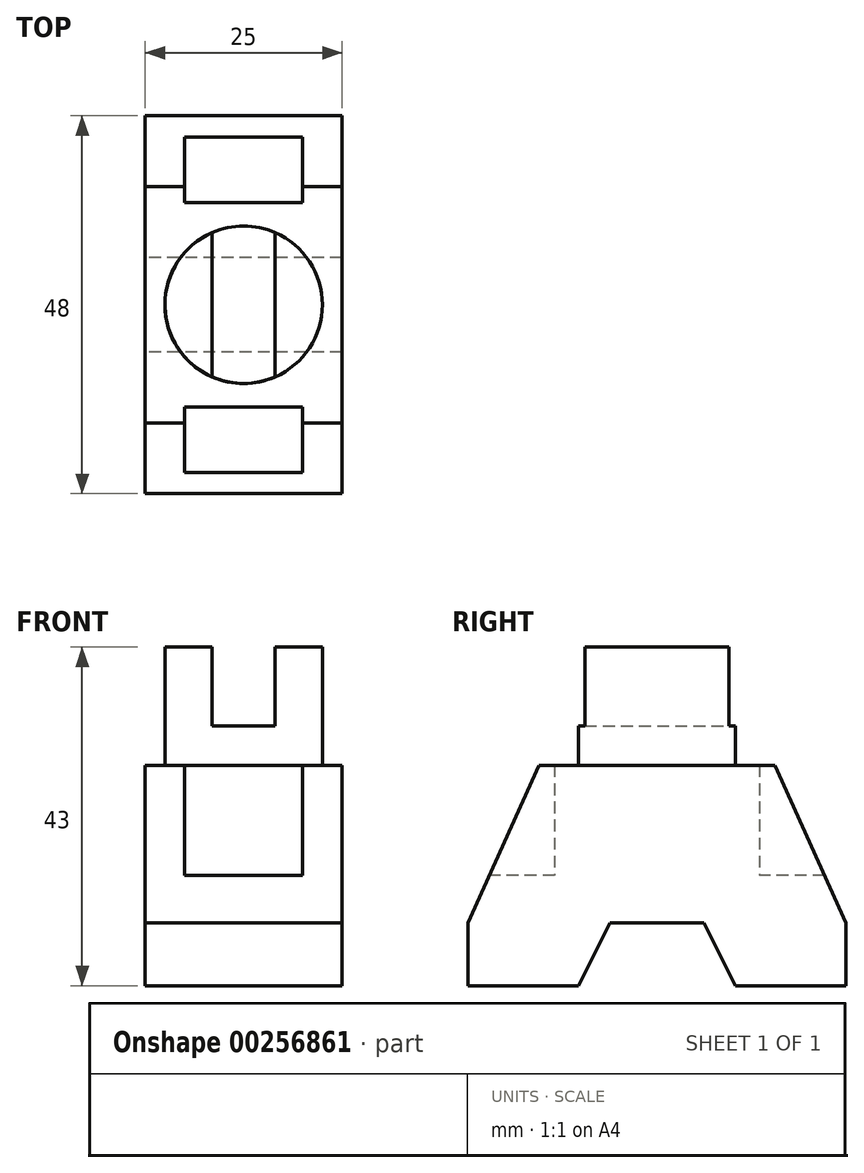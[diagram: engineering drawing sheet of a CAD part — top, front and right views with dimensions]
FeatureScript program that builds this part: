
annotation { "Feature Type Name" : "Feature", "Feature Type Description" : "" }
export const myFeature = defineFeature(function(context is Context, id is Id, definition is map)
    precondition{}
    {
        {
            var Q0;
            Q0=qCreatedBy(makeId("Right.planeOp"),FACE);
            var sketch = newSketch(context, id + "F0", { "sketchPlane" : qUnion([Q0])});
            skLineSegment(sketch, "E0.bottom", {"start": v(24, 14) * mm, "end": v(-24, 14) * mm});
            skLineSegment(sketch, "E0.top", {"start": v(24, -14) * mm, "end": v(-24, -14) * mm});
            skLineSegment(sketch, "E0.left", {"start": v(24, 14) * mm, "end": v(24, -14) * mm});
            skLineSegment(sketch, "E0.right", {"start": v(-24, 14) * mm, "end": v(-24, -14) * mm});
            skPoint(sketch, "E0.middle", {"position": v(0, 0) * mm});
            skLineSegment(sketch, "E1", {"start": v(-15, 14) * mm, "end": v(-15, -14) * mm});
            skLineSegment(sketch, "E2", {"start": v(-10, 14) * mm, "end": v(-10, -14) * mm});
            skLineSegment(sketch, "E3", {"start": v(15, 14) * mm, "end": v(15, -14) * mm});
            skLineSegment(sketch, "E4", {"start": v(10, 14) * mm, "end": v(10, -14) * mm});
            skLineSegment(sketch, "E5", {"start": v(-24, -4) * mm, "end": v(24, -4) * mm});
            skLineSegment(sketch, "E6", {"start": v(-24, -6) * mm, "end": v(24, -6) * mm});
            skLineSegment(sketch, "E7", {"start": v(-24, -6) * mm, "end": v(-15, 14) * mm});
            skLineSegment(sketch, "E8", {"start": v(24, -6) * mm, "end": v(15, 14) * mm});
            skLineSegment(sketch, "E9", {"start": v(-5, 14) * mm, "end": v(-5, -14) * mm});
            skLineSegment(sketch, "E10", {"start": v(5, 14) * mm, "end": v(5, -14) * mm});
            skLineSegment(sketch, "E11", {"start": v(-10, -14) * mm, "end": v(-5, -4) * mm});
            skLineSegment(sketch, "E12", {"start": v(10, -14) * mm, "end": v(5, -4) * mm});
            skSolve(sketch);
        }
        {
            var Q0;
            {var subQ0=sQuery(id+"F0.wireOp",EDGE,"E0.right");var subQ1=sQuery(id+"F0.wireOp",EDGE,"E0.top");var subQ2=makeQuery(id+"F0.imprint","INTERSECT",VERTEX,{"derivedFrom":[subQ1,subQ0]});Q0=makeQuery(id+"F0.imprint","IMPRINT",FACE,{"disambiguationData":[TD([[makeQuery(id+"F0.imprint","IMPRINT",EDGE,{"disambiguationData":[TD([[subQ2,1.0]])],"derivedFrom":subQ1}),-1.0]])]});}
            var Q1;
            {var subQ0=sQuery(id+"F0.wireOp",EDGE,"E5");var subQ1=sQuery(id+"F0.wireOp",EDGE,"E1");var subQ2=makeQuery(id+"F0.imprint","INTERSECT",VERTEX,{"derivedFrom":[subQ1,subQ0]});Q1=makeQuery(id+"F0.imprint","IMPRINT",FACE,{"disambiguationData":[TD([[makeQuery(id+"F0.imprint","IMPRINT",EDGE,{"disambiguationData":[TD([[subQ2,-1.0]])],"derivedFrom":subQ1}),-1.0]])]});}
            var Q2;
            {var subQ1=sQuery(id+"F0.wireOp",EDGE,"E1");var subQ3=sQuery(id+"F0.wireOp",EDGE,"E5");var subQ4=makeQuery(id+"F0.imprint","INTERSECT",VERTEX,{"derivedFrom":[subQ1,subQ3]});Q2=makeQuery(id+"F0.imprint","IMPRINT",FACE,{"disambiguationData":[TD([[makeQuery(id+"F0.imprint","IMPRINT",EDGE,{"disambiguationData":[TD([[subQ4,1.0]])],"derivedFrom":subQ3}),1.0]])]});}
            var Q3;
            {var subQ1=sQuery(id+"F0.wireOp",EDGE,"E0.bottom");var subQ3=sQuery(id+"F0.wireOp",EDGE,"E2");var subQ4=makeQuery(id+"F0.imprint","INTERSECT",VERTEX,{"derivedFrom":[subQ1,subQ3]});Q3=makeQuery(id+"F0.imprint","IMPRINT",FACE,{"disambiguationData":[TD([[makeQuery(id+"F0.imprint","IMPRINT",EDGE,{"disambiguationData":[TD([[subQ4,-1.0]])],"derivedFrom":subQ3}),-1.0]])]});}
            var Q4;
            {var subQ0=sQuery(id+"F0.wireOp",EDGE,"E2");var subQ1=sQuery(id+"F0.wireOp",EDGE,"E0.bottom");var subQ2=makeQuery(id+"F0.imprint","INTERSECT",VERTEX,{"derivedFrom":[subQ1,subQ0]});Q4=makeQuery(id+"F0.imprint","IMPRINT",FACE,{"disambiguationData":[TD([[makeQuery(id+"F0.imprint","IMPRINT",EDGE,{"disambiguationData":[TD([[subQ2,1.0]])],"derivedFrom":subQ1}),1.0]])]});}
            var Q5;
            {var subQ0=sQuery(id+"F0.wireOp",EDGE,"E9");var subQ1=sQuery(id+"F0.wireOp",EDGE,"E0.bottom");var subQ2=makeQuery(id+"F0.imprint","INTERSECT",VERTEX,{"derivedFrom":[subQ1,subQ0]});Q5=makeQuery(id+"F0.imprint","IMPRINT",FACE,{"disambiguationData":[TD([[makeQuery(id+"F0.imprint","IMPRINT",EDGE,{"disambiguationData":[TD([[subQ2,1.0]])],"derivedFrom":subQ1}),1.0]])]});}
            var Q6;
            {var subQ0=sQuery(id+"F0.wireOp",EDGE,"E4");var subQ1=sQuery(id+"F0.wireOp",EDGE,"E0.bottom");var subQ2=makeQuery(id+"F0.imprint","INTERSECT",VERTEX,{"derivedFrom":[subQ1,subQ0]});Q6=makeQuery(id+"F0.imprint","IMPRINT",FACE,{"disambiguationData":[TD([[makeQuery(id+"F0.imprint","IMPRINT",EDGE,{"disambiguationData":[TD([[subQ2,-1.0]])],"derivedFrom":subQ1}),1.0]])]});}
            var Q7;
            {var subQ1=sQuery(id+"F0.wireOp",EDGE,"E0.bottom");var subQ3=sQuery(id+"F0.wireOp",EDGE,"E4");var subQ4=makeQuery(id+"F0.imprint","INTERSECT",VERTEX,{"derivedFrom":[subQ1,subQ3]});Q7=makeQuery(id+"F0.imprint","IMPRINT",FACE,{"disambiguationData":[TD([[makeQuery(id+"F0.imprint","IMPRINT",EDGE,{"disambiguationData":[TD([[subQ4,-1.0]])],"derivedFrom":subQ3}),1.0]])]});}
            var Q8;
            {var subQ1=sQuery(id+"F0.wireOp",EDGE,"E3");var subQ3=sQuery(id+"F0.wireOp",EDGE,"E5");var subQ4=makeQuery(id+"F0.imprint","INTERSECT",VERTEX,{"derivedFrom":[subQ1,subQ3]});Q8=makeQuery(id+"F0.imprint","IMPRINT",FACE,{"disambiguationData":[TD([[makeQuery(id+"F0.imprint","IMPRINT",EDGE,{"disambiguationData":[TD([[subQ4,-1.0]])],"derivedFrom":subQ3}),1.0]])]});}
            var Q9;
            {var subQ0=sQuery(id+"F0.wireOp",EDGE,"E5");var subQ1=sQuery(id+"F0.wireOp",EDGE,"E3");var subQ2=makeQuery(id+"F0.imprint","INTERSECT",VERTEX,{"derivedFrom":[subQ1,subQ0]});Q9=makeQuery(id+"F0.imprint","IMPRINT",FACE,{"disambiguationData":[TD([[makeQuery(id+"F0.imprint","IMPRINT",EDGE,{"disambiguationData":[TD([[subQ2,-1.0]])],"derivedFrom":subQ1}),1.0]])]});}
            var Q10;
            {var subQ0=sQuery(id+"F0.wireOp",EDGE,"E0.left");var subQ1=sQuery(id+"F0.wireOp",EDGE,"E0.top");var subQ2=makeQuery(id+"F0.imprint","INTERSECT",VERTEX,{"derivedFrom":[subQ1,subQ0]});Q10=makeQuery(id+"F0.imprint","IMPRINT",FACE,{"disambiguationData":[TD([[makeQuery(id+"F0.imprint","IMPRINT",EDGE,{"disambiguationData":[TD([[subQ2,-1.0]])],"derivedFrom":subQ1}),-1.0]])]});}
            var Q11;
            {var subQ0=sQuery(id+"F0.wireOp",EDGE,"E3");var subQ1=sQuery(id+"F0.wireOp",EDGE,"E0.top");var subQ2=makeQuery(id+"F0.imprint","INTERSECT",VERTEX,{"derivedFrom":[subQ1,subQ0]});Q11=makeQuery(id+"F0.imprint","IMPRINT",FACE,{"disambiguationData":[TD([[makeQuery(id+"F0.imprint","IMPRINT",EDGE,{"disambiguationData":[TD([[subQ2,1.0]])],"derivedFrom":subQ0}),-1.0]])]});}
            var Q12;
            {var subQ1=sQuery(id+"F0.wireOp",EDGE,"E4");var subQ3=sQuery(id+"F0.wireOp",EDGE,"E6");var subQ4=makeQuery(id+"F0.imprint","INTERSECT",VERTEX,{"derivedFrom":[subQ1,subQ3]});Q12=makeQuery(id+"F0.imprint","IMPRINT",FACE,{"disambiguationData":[TD([[makeQuery(id+"F0.imprint","IMPRINT",EDGE,{"disambiguationData":[TD([[subQ4,1.0]])],"derivedFrom":subQ3}),-1.0]])]});}
            var Q13;
            {var subQ0=sQuery(id+"F0.wireOp",EDGE,"E5");var subQ1=sQuery(id+"F0.wireOp",EDGE,"E3");var subQ2=makeQuery(id+"F0.imprint","INTERSECT",VERTEX,{"derivedFrom":[subQ1,subQ0]});Q13=makeQuery(id+"F0.imprint","IMPRINT",FACE,{"disambiguationData":[TD([[makeQuery(id+"F0.imprint","IMPRINT",EDGE,{"disambiguationData":[TD([[subQ2,-1.0]])],"derivedFrom":subQ1}),-1.0]])]});}
            var Q14;
            {var subQ0=sQuery(id+"F0.wireOp",EDGE,"E9");var subQ5=sQuery(id+"F0.wireOp",EDGE,"E6");var subQ6=makeQuery(id+"F0.imprint","INTERSECT",VERTEX,{"derivedFrom":[subQ5,subQ0]});Q14=makeQuery(id+"F0.imprint","IMPRINT",FACE,{"disambiguationData":[TD([[makeQuery(id+"F0.imprint","IMPRINT",EDGE,{"disambiguationData":[TD([[subQ6,-1.0]])],"derivedFrom":subQ5}),1.0]])]});}
            var Q15;
            {var subQ0=sQuery(id+"F0.wireOp",EDGE,"E11");var subQ1=sQuery(id+"F0.wireOp",EDGE,"E6");var subQ2=makeQuery(id+"F0.imprint","INTERSECT",VERTEX,{"derivedFrom":[subQ1,subQ0]});Q15=makeQuery(id+"F0.imprint","IMPRINT",FACE,{"disambiguationData":[TD([[makeQuery(id+"F0.imprint","IMPRINT",EDGE,{"disambiguationData":[TD([[subQ2,-1.0]])],"derivedFrom":subQ1}),1.0]])]});}
            var Q16;
            {var subQ0=sQuery(id+"F0.wireOp",EDGE,"E10");var subQ1=sQuery(id+"F0.wireOp",EDGE,"E6");var subQ2=makeQuery(id+"F0.imprint","INTERSECT",VERTEX,{"derivedFrom":[subQ1,subQ0]});Q16=makeQuery(id+"F0.imprint","IMPRINT",FACE,{"disambiguationData":[TD([[makeQuery(id+"F0.imprint","IMPRINT",EDGE,{"disambiguationData":[TD([[subQ2,-1.0]])],"derivedFrom":subQ1}),1.0]])]});}
            var Q17;
            {var subQ0=sQuery(id+"F0.wireOp",EDGE,"E5");var subQ1=sQuery(id+"F0.wireOp",EDGE,"E4");var subQ2=makeQuery(id+"F0.imprint","INTERSECT",VERTEX,{"derivedFrom":[subQ1,subQ0]});Q17=makeQuery(id+"F0.imprint","IMPRINT",FACE,{"disambiguationData":[TD([[makeQuery(id+"F0.imprint","IMPRINT",EDGE,{"disambiguationData":[TD([[subQ2,-1.0]])],"derivedFrom":subQ1}),-1.0]])]});}
            var Q18;
            {var subQ0=sQuery(id+"F0.wireOp",EDGE,"E5");var subQ1=sQuery(id+"F0.wireOp",EDGE,"E2");var subQ2=makeQuery(id+"F0.imprint","INTERSECT",VERTEX,{"derivedFrom":[subQ1,subQ0]});Q18=makeQuery(id+"F0.imprint","IMPRINT",FACE,{"disambiguationData":[TD([[makeQuery(id+"F0.imprint","IMPRINT",EDGE,{"disambiguationData":[TD([[subQ2,-1.0]])],"derivedFrom":subQ1}),1.0]])]});}
            var Q19;
            {var subQ1=sQuery(id+"F0.wireOp",EDGE,"E2");var subQ3=sQuery(id+"F0.wireOp",EDGE,"E6");var subQ4=makeQuery(id+"F0.imprint","INTERSECT",VERTEX,{"derivedFrom":[subQ1,subQ3]});Q19=makeQuery(id+"F0.imprint","IMPRINT",FACE,{"disambiguationData":[TD([[makeQuery(id+"F0.imprint","IMPRINT",EDGE,{"disambiguationData":[TD([[subQ4,-1.0]])],"derivedFrom":subQ3}),-1.0]])]});}
            var Q20;
            {var subQ0=sQuery(id+"F0.wireOp",EDGE,"E1");var subQ1=sQuery(id+"F0.wireOp",EDGE,"E0.top");var subQ2=makeQuery(id+"F0.imprint","INTERSECT",VERTEX,{"derivedFrom":[subQ1,subQ0]});Q20=makeQuery(id+"F0.imprint","IMPRINT",FACE,{"disambiguationData":[TD([[makeQuery(id+"F0.imprint","IMPRINT",EDGE,{"disambiguationData":[TD([[subQ2,1.0]])],"derivedFrom":subQ0}),1.0]])]});}
            var Q21;
            {var subQ0=sQuery(id+"F0.wireOp",EDGE,"E5");var subQ1=sQuery(id+"F0.wireOp",EDGE,"E1");var subQ2=makeQuery(id+"F0.imprint","INTERSECT",VERTEX,{"derivedFrom":[subQ1,subQ0]});Q21=makeQuery(id+"F0.imprint","IMPRINT",FACE,{"disambiguationData":[TD([[makeQuery(id+"F0.imprint","IMPRINT",EDGE,{"disambiguationData":[TD([[subQ2,-1.0]])],"derivedFrom":subQ1}),1.0]])]});}
            extrude(context, id + "F1", {"entities" : qUnion([Q0, Q1, Q2, Q3, Q4, Q5, Q6, Q7, Q8, Q9, Q10, Q11, Q12, Q13, Q14, Q15, Q16, Q17, Q18, Q19, Q20, Q21]), "endBound" : BoundingType.SYMMETRIC, "depth" : 25 * mm});
        }
        {
            var Q0;
            Q0=makeQuery(id+"F1.opExtrude","SWEPT_FACE",FACE,{"disambiguationData":[OSD([sQuery(id+"F0.wireOp",EDGE,"E0.bottom")])]});
            var sketch = newSketch(context, id + "F2", { "sketchPlane" : qUnion([Q0])});
            skCircle(sketch, "E13", {"center": v(0, 0) * mm, "radius": 10 * mm});
            skSolve(sketch);
        }
        {
            var Q0;
            Q0=makeQuery(id+"F2.imprint","IMPRINT",FACE,{"disambiguationData":[TD([[makeQuery(id+"F2.imprint","IMPRINT",EDGE,{"derivedFrom":sQuery(id+"F2.wireOp",EDGE,"E13")}),1.0]])]});
            extrude(context, id + "F3", {"entities" : qUnion([Q0]), "operationType" : NewBodyOperationType.ADD, "depth" : 15 * mm});
        }
        {
            var Q0;
            Q0=makeQuery(id+"F3.opExtrude","CAP_FACE",FACE,{"disambiguationData":[OSD([sQuery(id+"F2.wireOp",EDGE,"E13")])],"isStart":false});
            var sketch = newSketch(context, id + "F4", { "sketchPlane" : qUnion([Q0])});
            skLineSegment(sketch, "E14.bottom", {"start": v(-10, 10) * mm, "end": v(10, 10) * mm});
            skLineSegment(sketch, "E14.top", {"start": v(-10, -10) * mm, "end": v(10, -10) * mm});
            skLineSegment(sketch, "E14.left", {"start": v(-10, 10) * mm, "end": v(-10, -10) * mm});
            skLineSegment(sketch, "E14.right", {"start": v(10, 10) * mm, "end": v(10, -10) * mm});
            skPoint(sketch, "E14.middle", {"position": v(0, 0) * mm});
            skLineSegment(sketch, "E15", {"start": v(-4, -9.17) * mm, "end": v(-4, 9.17) * mm});
            skLineSegment(sketch, "E16", {"start": v(4, -9.17) * mm, "end": v(4, 9.17) * mm});
            skSolve(sketch);
        }
        {
            var Q0;
            {var subQ1=sQuery(id+"F4.wireOp",EDGE,"E15");Q0=makeQuery(id+"F4.imprint","IMPRINT",FACE,{"disambiguationData":[TD([[makeQuery(id+"F4.imprint","IMPRINT",EDGE,{"derivedFrom":subQ1}),-1.0]])]});}
            extrude(context, id + "F5", {"entities" : qUnion([Q0]), "operationType" : NewBodyOperationType.REMOVE, "oppositeDirection" : true, "depth" : 10 * mm});
        }
        {
            var Q0;
            Q0=qCreatedBy(makeId("Top.planeOp"),FACE);
            var sketch = newSketch(context, id + "F6", { "sketchPlane" : qUnion([Q0])});
            skLineSegment(sketch, "E17.bottom", {"start": v(12.5, -24) * mm, "end": v(-12.5, -24) * mm});
            skLineSegment(sketch, "E17.top", {"start": v(12.5, 24) * mm, "end": v(-12.5, 24) * mm});
            skLineSegment(sketch, "E17.left", {"start": v(12.5, -24) * mm, "end": v(12.5, 24) * mm});
            skLineSegment(sketch, "E17.right", {"start": v(-12.5, -24) * mm, "end": v(-12.5, 24) * mm});
            skPoint(sketch, "E17.middle", {"position": v(0, 0) * mm});
            skLineSegment(sketch, "E18", {"start": v(12.5, 13) * mm, "end": v(-12.5, 13) * mm});
            skLineSegment(sketch, "E19", {"start": v(12.5, -13) * mm, "end": v(-12.5, -13) * mm});
            skLineSegment(sketch, "E20", {"start": v(12.5, -21.3) * mm, "end": v(-12.5, -21.3) * mm});
            skLineSegment(sketch, "E21", {"start": v(12.5, 21.3) * mm, "end": v(-12.5, 21.3) * mm});
            skLineSegment(sketch, "E22", {"start": v(7.5, 24) * mm, "end": v(7.5, -24) * mm});
            skLineSegment(sketch, "E23", {"start": v(-7.5, 24) * mm, "end": v(-7.5, -24) * mm});
            skSolve(sketch);
        }
        {
            var Q0;
            {var subQ0=sQuery(id+"F6.wireOp",EDGE,"E22");var subQ1=sQuery(id+"F6.wireOp",EDGE,"E19");var subQ2=makeQuery(id+"F6.imprint","INTERSECT",VERTEX,{"derivedFrom":[subQ1,subQ0]});Q0=makeQuery(id+"F6.imprint","IMPRINT",FACE,{"disambiguationData":[TD([[makeQuery(id+"F6.imprint","IMPRINT",EDGE,{"disambiguationData":[TD([[subQ2,-1.0]])],"derivedFrom":subQ1}),1.0]])]});}
            var Q1;
            {var subQ0=sQuery(id+"F6.wireOp",EDGE,"E22");var subQ1=sQuery(id+"F6.wireOp",EDGE,"E18");var subQ2=makeQuery(id+"F6.imprint","INTERSECT",VERTEX,{"derivedFrom":[subQ1,subQ0]});Q1=makeQuery(id+"F6.imprint","IMPRINT",FACE,{"disambiguationData":[TD([[makeQuery(id+"F6.imprint","IMPRINT",EDGE,{"disambiguationData":[TD([[subQ2,-1.0]])],"derivedFrom":subQ1}),-1.0]])]});}
            extrude(context, id + "F7", {"entities" : qUnion([Q0, Q1]), "operationType" : NewBodyOperationType.REMOVE, "depth" : 14 * mm});
        }
    });
